# Revit family: Kro Kanalkryss - Kro-X
name_source: partatom
category: Duct Accessories
units: mm (PartAtom-declared; Revit-internal decimal feet)

## family parameters
Always vertical = Yes
Cut with Voids When Loaded = Yes
Part Type = Breaks Into
Round Connector Dimension = Use Diameter
Shared = Yes
Work Plane-Based = No

## types (23) — shared parameters
Bredde Kvadrat = 150 mm
D4 - Bredde senterkanal = 360 mm  [stored 1.1811 ft]
Description = Våre kanalkryss gir kun 7 Pa i trykkfall, i begge rør, ved en hastighet på 7 m/s. Ingen lyd ved 5-10 m/s i kanalene.
Manufacturer = Kro Produksjon AS
Model = KroX
URL = www.kroproduksjon.no

## per-type parameters (varying)
| type | D1 - Dimensjon til senterkanal | D2 - Dimensjon tilkoplingspunkter | L2 - Total lengde |
| 125/100-R | 125 mm  [stored 0.410105 ft] | 100 mm  [stored 0.328084 ft] | 395 mm  [stored 1.29593 ft] |
| 125/125-R | 125 mm  [stored 0.410105 ft] | 125 mm  [stored 0.410105 ft] | 495 mm  [stored 1.62402 ft] |
| 160/100-R | 160 mm  [stored 0.524934 ft] | 100 mm  [stored 0.328084 ft] | 530 mm  [stored 1.73885 ft] |
| 160/125-R | 160 mm  [stored 0.524934 ft] | 125 mm  [stored 0.410105 ft] | 530 mm  [stored 1.73885 ft] |
| 160/160-R | 160 mm  [stored 0.524934 ft] | 160 mm  [stored 0.524934 ft] | 740 mm  [stored 2.42782 ft] |
| 200/125-R | 200 mm  [stored 0.656168 ft] | 125 mm  [stored 0.410105 ft] | 570 mm  [stored 1.87008 ft] |
| 200/160-R | 200 mm  [stored 0.656168 ft] | 160 mm  [stored 0.524934 ft] | 640 mm  [stored 2.09974 ft] |
| 250/125-R | 250 mm  [stored 0.82021 ft] | 125 mm  [stored 0.410105 ft] | 620 mm  [stored 2.03412 ft] |
| 250/160-R | 250 mm  [stored 0.82021 ft] | 160 mm  [stored 0.524934 ft] | 640 mm  [stored 2.09974 ft] |
| 250/200-R | 250 mm  [stored 0.82021 ft] | 200 mm  [stored 0.656168 ft] | 720 mm  [stored 2.3622 ft] |
| 315/160-R | 315 mm  [stored 1.03346 ft] | 160 mm  [stored 0.524934 ft] | 705 mm  [stored 2.31299 ft] |
| 315/200-R | 315 mm  [stored 1.03346 ft] | 200 mm  [stored 0.656168 ft] | 785 mm |
| 315/250-R | 315 mm  [stored 1.03346 ft] | 250 mm  [stored 0.82021 ft] | 945 mm  [stored 3.10039 ft] |
| 400/200-R | 400 mm  [stored 1.31234 ft] | 200 mm  [stored 0.656168 ft] | 870 mm  [stored 2.85433 ft] |
| 400/250-R | 400 mm  [stored 1.31234 ft] | 250 mm  [stored 0.82021 ft] | 1030 mm  [stored 3.37927 ft] |
| 400/315-R | 400 mm  [stored 1.31234 ft] | 315 mm  [stored 1.03346 ft] | 1160 mm  [stored 3.80577 ft] |
| 500/200-R | 500 mm  [stored 1.64042 ft] | 200 mm  [stored 0.656168 ft] | 970 mm  [stored 3.18241 ft] |
| 500/250-R | 500 mm  [stored 1.64042 ft] | 250 mm  [stored 0.82021 ft] | 1130 mm  [stored 3.70735 ft] |
| 500/315-R | 500 mm  [stored 1.64042 ft] | 315 mm  [stored 1.03346 ft] | 1260 mm  [stored 4.13386 ft] |
| 630/315-R | 630 mm  [stored 2.06693 ft] | 315 mm  [stored 1.03346 ft] | 1390 mm  [stored 4.56037 ft] |
| 630/400-R | 630 mm  [stored 2.06693 ft] | 400 mm  [stored 1.31234 ft] | 1580 mm  [stored 5.18373 ft] |
| 800/400-R | 800 mm  [stored 2.62467 ft] | 400 mm  [stored 1.31234 ft] | 1730 mm  [stored 5.67585 ft] |
| 800/500-R | 800 mm  [stored 2.62467 ft] | 500 mm  [stored 1.64042 ft] | 1960 mm  [stored 6.43045 ft] |

note: [stored X ft] marks values corroborated as IEEE doubles in the binary element streams (Revit-internal decimal feet)

## geometry (parser evidence)
native form markers: Sweep x2
no freeform markers — native parametric forms only
